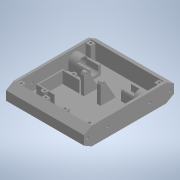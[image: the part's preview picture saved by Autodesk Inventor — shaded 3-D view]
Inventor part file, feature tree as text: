
AUTODESK INVENTOR PART (.ipt)
format: ipt  version: 2020 (Build 240168000, 168)  size: 474,112 bytes
history: native  units: in
note: dims shown in document units (in); Inventor stores cm internally (conversion verified against a paired STEP export)
features: extrude x14, sketch x14, projected_geometry x14, mirror x4, plane x1
ambient origin geometry x8: Origin, YZ Plane, XZ Plane, XY Plane, X Axis, Y Axis, Z Axis, Center Point
bodies: Solid1 (feature_tree)
feature tree (47):
  extrude  "Extrusion1"  Depth=5.9055in
  extrude  "Extrusion2"  TaperAngle=0.0deg  [1 undecoded]
  extrude  "Extrusion3"  Depth=1.063in
  extrude  "Extrusion4"  Depth=0.315in
  extrude  "Extrusion5"  TaperAngle=0.0deg  [1 undecoded]
  extrude  "Extrusion6"  Depth=0.5906in
  mirror  "Mirror1"
  extrude  "Extrusion7"  Depth=0.0787in
  mirror  "Mirror2"
  extrude  "Extrusion8"  Depth=0.6102in
  mirror  "Mirror3"
  plane  "Work Plane1"
  extrude  "Extrusion9"  Depth=0.7874in TaperAngle=0.0deg
  mirror  "Mirror4"
  extrude  "Extrusion10"  Depth=6.063in TaperAngle=0.0deg
  extrude  "Extrusion11"  Depth=0.1575in
  extrude  "Extrusion12"  TaperAngle=0.0deg  [1 undecoded]
  extrude  "Extrusion13"  Depth=0.2756in
  extrude  "Extrusion14"  Depth=0.4331in
  sketch  "Sketch1"  dims[d0=1.1811in d1=5.9055in]
  sketch  "Sketch2"  dims[d2=5.1181in d3=0.0in]
  projected_geometry  "Projected Loop1"
  sketch  "Sketch3"  dims[d4=0.1575in d5=1.063in]
  projected_geometry  "Projected Loop2"
  projected_geometry  "Projected Loop3"
  sketch  "Sketch4"  dims[d6=0.0in d8=0.315in]
  sketch  "Sketch5"  dims[d10=0.993in d11=0.0in]
  projected_geometry  "Projected Loop4"
  sketch  "Sketch6"  dims[d12=0.6496in d13=0.5906in]
  sketch  "Sketch7"  dims[d14=1.5748in d15=0.0787in]
  sketch  "Sketch9"  dims[d16=0.5512in d17=0.0in d18=0.6102in]
  sketch  "Sketch10"  dims[d19=0.4803in d20=0.7874in d21=0.0in]
  sketch  "Sketch12"  dims[d22=0.1654in d23=6.063in d24=0.0in]
  projected_geometry  "Projected Loop6"
  projected_geometry  "Projected Loop7"
  projected_geometry  "Projected Loop8"
  sketch  "Sketch13"  dims[d25=0.5114in d26=0.1575in]
  projected_geometry  "Projected Loop9"
  projected_geometry  "Projected Loop10"
  projected_geometry  "Projected Loop11"
  projected_geometry  "Projected Loop12"
  projected_geometry  "Projected Loop13"
  projected_geometry  "Projected Loop14"
  sketch  "Sketch14"  dims[d27=1.5748in d28=0.0in d29=0.0in]
  sketch  "Sketch15"  dims[d30=0.1575in d31=0.2756in]
  projected_geometry  "Projected Loop15"
  sketch  "Sketch16"  dims[d32=0.0in d33=0.4331in d34=0.122in d38=2.7559in d40=0.061in d41=0.0909in d42=0.2362in d43=0.0in d44=60.0deg d45=0.0787in d46=0.315in d48=0.993in d49=0.0in d51=0.1575in d52=0.1575in d53=0.2756in d54=0.0in d55=0.4724in d56=1.1614in d57=1.5748in d58=1.5945in d59=0.0787in d60=0.0787in d62=0.315in d63=0.7677in d64=0.0in d65=0.1575in d66=0.1575in d67=0.2756in d68=0.0in d69=0.8268in d70=0.2953in d71=0.0394in d72=0.0in]
note: 3 required parameter values undecoded (feature->parameter linkage not recoverable at this tier; creation-order binding heuristic only, values carry confidence <= 0.55)
